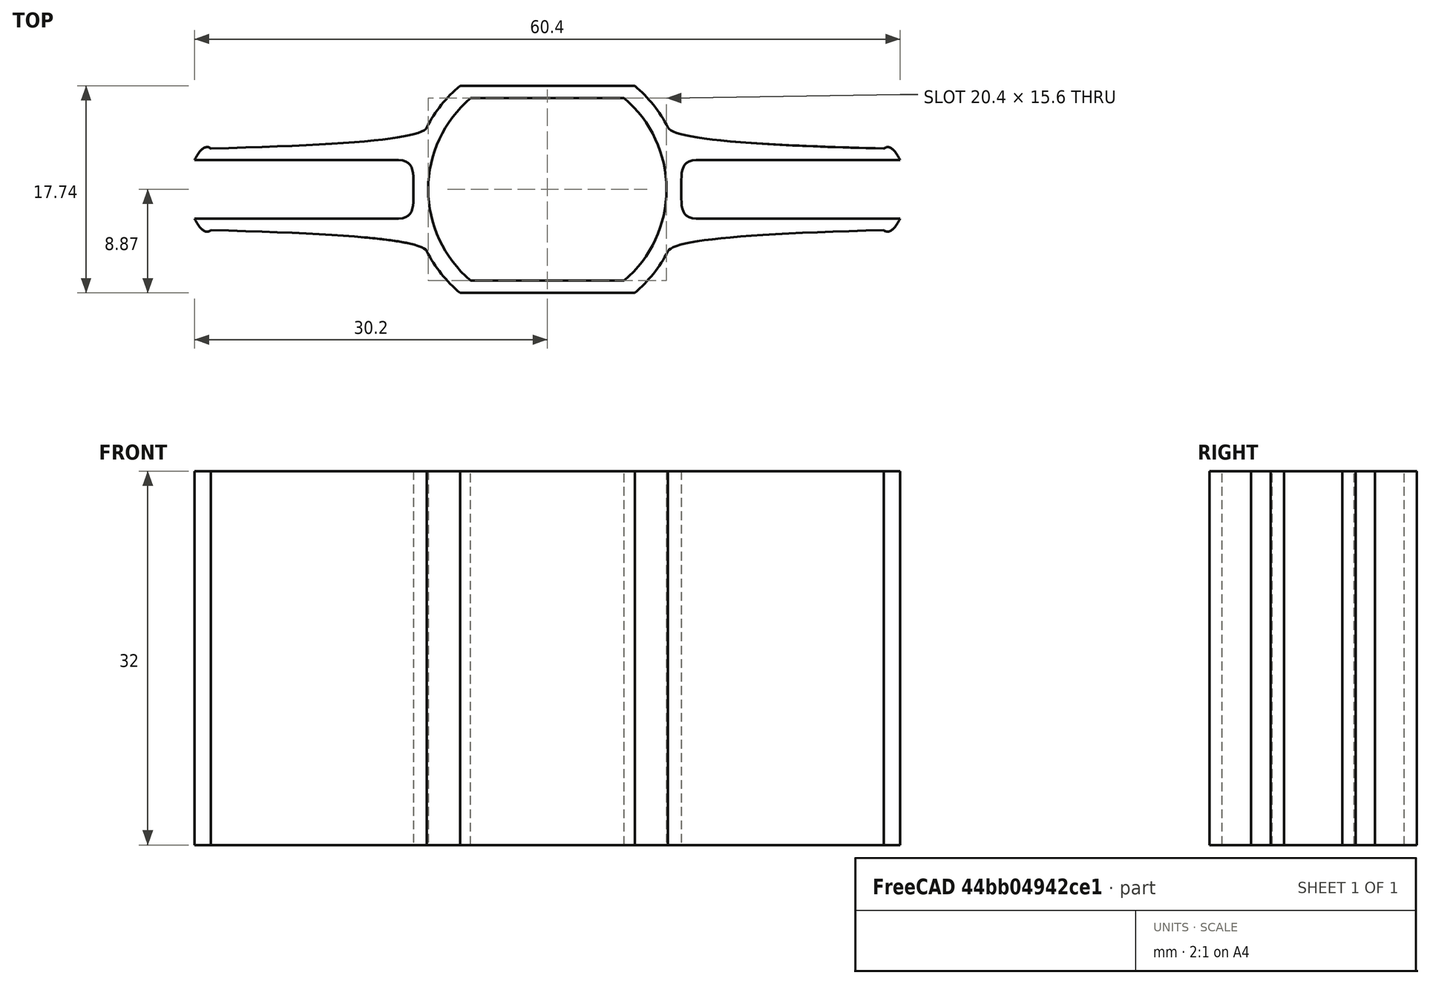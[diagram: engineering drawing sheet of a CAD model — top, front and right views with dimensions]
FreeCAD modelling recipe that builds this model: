
FCSTD DOCUMENT  (FreeCAD 0.19R0.19.2)
Label: 017
License: All rights reserved
LicenseURL: http://en.wikipedia.org/wiki/All_rights_reserved
objects: Sketcher::SketchObject×2, Part::Extrusion×1
note: 3 computed .brp shape members not serialized (recipe doc carries the construction recipe); baked Part::Feature solids carry a one-line shape summary decoded from their .brp

FEATURE [Sketcher::SketchObject] Sketch  label="main001"
  FullyConstrained = true
  sketch-geometry (80):
    g0: ArcOfCircle CenterX=-3.45031e-07 CenterY=0 CenterZ=0 NormalX=0 NormalY=0 NormalZ=1 AngleXU=0 Radius=10.2 StartAngle=5.4126 EndAngle=7.15377
    g1: ArcOfCircle CenterX=-3.45031e-07 CenterY=0 CenterZ=0 NormalX=0 NormalY=0 NormalZ=1 AngleXU=0 Radius=10.2 StartAngle=2.27101 EndAngle=4.01218
    g2: LineSegment StartX=-6.57267 StartY=7.8 StartZ=0 EndX=6.57267 EndY=7.8 EndZ=0
    g3: LineSegment StartX=-6.57267 StartY=-7.8 StartZ=0 EndX=6.57267 EndY=-7.8 EndZ=0
    g4: ArcOfCircle CenterX=-3.45031e-07 CenterY=0 CenterZ=0 NormalX=0 NormalY=0 NormalZ=1 AngleXU=0 Radius=11.6 StartAngle=2.27101 EndAngle=2.66709
    g5: ArcOfCircle CenterX=-3.45031e-07 CenterY=0 CenterZ=0 NormalX=0 NormalY=0 NormalZ=1 AngleXU=0 Radius=11.6 StartAngle=5.4126 EndAngle=5.80868
    g6: LineSegment StartX=-7.4748 StartY=8.87059 StartZ=0 EndX=7.4748 EndY=8.87059 EndZ=0
    g7: LineSegment StartX=-7.4748 StartY=-8.87059 StartZ=0 EndX=7.4748 EndY=-8.87059 EndZ=0
    g8: ArcOfCircle CenterX=-3.45031e-07 CenterY=0 CenterZ=0 NormalX=0 NormalY=0 NormalZ=1 AngleXU=0 Radius=11.6 StartAngle=3.6161 EndAngle=4.01218
    g9: ArcOfCircle CenterX=-3.45031e-07 CenterY=0 CenterZ=0 NormalX=0 NormalY=0 NormalZ=1 AngleXU=0 Radius=11.6 StartAngle=0.474503 EndAngle=0.870585
    g10: Circle CenterX=-28.8 CenterY=3.5 CenterZ=0 NormalX=0 NormalY=0 NormalZ=1 AngleXU=0 Radius=1
    g11: Circle CenterX=-10.9247 CenterY=3.9 CenterZ=0 NormalX=0 NormalY=0 NormalZ=1 AngleXU=0 Radius=1
    g12: Circle CenterX=-10.3184 CenterY=5.3 CenterZ=0 NormalX=0 NormalY=0 NormalZ=1 AngleXU=0 Radius=1
    g13: BSplineCurve PolesCount=3 KnotsCount=2 Degree=2 IsPeriodic=0
    g14: GeomPoint X=-28.8 Y=3.5 Z=0
    g15: GeomPoint X=-10.3184 Y=5.3 Z=0
    g16: Circle CenterX=28.8 CenterY=3.5 CenterZ=0 NormalX=0 NormalY=0 NormalZ=1 AngleXU=0 Radius=1
    g17: Circle CenterX=10.9247 CenterY=3.9 CenterZ=0 NormalX=0 NormalY=0 NormalZ=1 AngleXU=0 Radius=1
    g18: Circle CenterX=10.3184 CenterY=5.3 CenterZ=0 NormalX=0 NormalY=0 NormalZ=1 AngleXU=0 Radius=1
    g19: BSplineCurve PolesCount=3 KnotsCount=2 Degree=2 IsPeriodic=0
    g20: GeomPoint X=28.8 Y=3.5 Z=0
    g21: GeomPoint X=10.3184 Y=5.3 Z=0
    g22: Circle CenterX=-28.8 CenterY=-3.5 CenterZ=0 NormalX=0 NormalY=0 NormalZ=1 AngleXU=0 Radius=1
    g23: Circle CenterX=-10.9247 CenterY=-3.9 CenterZ=0 NormalX=0 NormalY=0 NormalZ=1 AngleXU=0 Radius=1
    g24: Circle CenterX=-10.3184 CenterY=-5.3 CenterZ=0 NormalX=0 NormalY=0 NormalZ=1 AngleXU=0 Radius=1
    g25: BSplineCurve PolesCount=3 KnotsCount=2 Degree=2 IsPeriodic=0
    g26: GeomPoint X=-28.8 Y=-3.5 Z=0
    g27: GeomPoint X=-10.3184 Y=-5.3 Z=0
    g28: Circle CenterX=28.8 CenterY=-3.5 CenterZ=0 NormalX=0 NormalY=0 NormalZ=1 AngleXU=0 Radius=1
    g29: Circle CenterX=10.9247 CenterY=-3.9 CenterZ=0 NormalX=0 NormalY=0 NormalZ=1 AngleXU=0 Radius=1
    g30: Circle CenterX=10.3184 CenterY=-5.3 CenterZ=0 NormalX=0 NormalY=0 NormalZ=1 AngleXU=0 Radius=1
    g31: BSplineCurve PolesCount=3 KnotsCount=2 Degree=2 IsPeriodic=0
    g32: GeomPoint X=28.8 Y=-3.5 Z=0
    g33: GeomPoint X=10.3184 Y=-5.3 Z=0
    g34-g38: Circle x5 (B-spline internal-alignment scaffolding for g39; pole/knot coordinates omitted)
    g39: BSplineCurve PolesCount=5 KnotsCount=3 Degree=3 IsPeriodic=0
    g40: GeomPoint X=12.7274 Y=2.5 Z=0
    g41: GeomPoint X=11.4637 Y=2.49999e-07 Z=0
    g42: GeomPoint X=12.7274 Y=-2.5 Z=0
    g43-g47: Circle x5 (B-spline internal-alignment scaffolding for g48; pole/knot coordinates omitted)
    g48: BSplineCurve PolesCount=5 KnotsCount=3 Degree=3 IsPeriodic=0
    g49: GeomPoint X=-12.7274 Y=2.5 Z=0
    g50: GeomPoint X=-11.4637 Y=2.50004e-07 Z=0
    g51: GeomPoint X=-12.7274 Y=-2.5 Z=0
    g52: LineSegment StartX=-30.2 StartY=-2.5 StartZ=0 EndX=-12.7274 EndY=-2.5 EndZ=0
    g53: LineSegment StartX=-30.2 StartY=2.5 StartZ=0 EndX=-12.7274 EndY=2.5 EndZ=0
    g54: LineSegment StartX=30.2 StartY=2.5 StartZ=0 EndX=12.7274 EndY=2.5 EndZ=0
    g55: LineSegment StartX=30.2 StartY=-2.5 StartZ=0 EndX=12.7274 EndY=-2.5 EndZ=0
    g56: Circle CenterX=-30.2 CenterY=2.5 CenterZ=0 NormalX=0 NormalY=0 NormalZ=1 AngleXU=0 Radius=1
    g57: Circle CenterX=-29.4304 CenterY=3.99253 CenterZ=0 NormalX=0 NormalY=0 NormalZ=1 AngleXU=0 Radius=1
    g58: Circle CenterX=-28.8 CenterY=3.5 CenterZ=0 NormalX=0 NormalY=0 NormalZ=1 AngleXU=0 Radius=1
    g59: BSplineCurve PolesCount=3 KnotsCount=2 Degree=2 IsPeriodic=0
    g60: GeomPoint X=-30.2 Y=2.5 Z=0
    g61: GeomPoint X=-28.8 Y=3.5 Z=0
    g62: Circle CenterX=30.2 CenterY=-2.5 CenterZ=0 NormalX=0 NormalY=0 NormalZ=1 AngleXU=0 Radius=1
    g63: Circle CenterX=29.4304 CenterY=-3.99253 CenterZ=0 NormalX=0 NormalY=0 NormalZ=1 AngleXU=0 Radius=1
    g64: Circle CenterX=28.8 CenterY=-3.5 CenterZ=0 NormalX=0 NormalY=0 NormalZ=1 AngleXU=0 Radius=1
    g65: BSplineCurve PolesCount=3 KnotsCount=2 Degree=2 IsPeriodic=0
    g66: GeomPoint X=30.2 Y=-2.5 Z=0
    g67: GeomPoint X=28.8 Y=-3.5 Z=0
    g68: Circle CenterX=30.2 CenterY=2.5 CenterZ=0 NormalX=0 NormalY=0 NormalZ=1 AngleXU=0 Radius=1
    g69: Circle CenterX=29.4304 CenterY=3.99253 CenterZ=0 NormalX=0 NormalY=0 NormalZ=1 AngleXU=0 Radius=1
    g70: Circle CenterX=28.8 CenterY=3.5 CenterZ=0 NormalX=0 NormalY=0 NormalZ=1 AngleXU=0 Radius=1
    g71: BSplineCurve PolesCount=3 KnotsCount=2 Degree=2 IsPeriodic=0
    g72: GeomPoint X=30.2 Y=2.5 Z=0
    g73: GeomPoint X=28.8 Y=3.5 Z=0
    g74: Circle CenterX=-30.2 CenterY=-2.5 CenterZ=0 NormalX=0 NormalY=0 NormalZ=1 AngleXU=0 Radius=1
    g75: Circle CenterX=-29.4304 CenterY=-3.99253 CenterZ=0 NormalX=0 NormalY=0 NormalZ=1 AngleXU=0 Radius=1
    g76: Circle CenterX=-28.8 CenterY=-3.5 CenterZ=0 NormalX=0 NormalY=0 NormalZ=1 AngleXU=0 Radius=1
    g77: BSplineCurve PolesCount=3 KnotsCount=2 Degree=2 IsPeriodic=0
    g78: GeomPoint X=-30.2 Y=-2.5 Z=0
    g79: GeomPoint X=-28.8 Y=-3.5 Z=0
  constraints (131):
    c: Block(g0)
    c: Equal(g0,g1)
    c: Coincident(g0,g1)
    c: Coincident(g2,g1)
    c: Coincident(g2,g0)
    c: Horizontal(g2)
    c: Coincident(g3,g1)
    c: Coincident(g3,g0)
    c: Horizontal(g3)
    c: Block(g2)
    c: Block(g3)
    c: Coincident(g4,g0)
    c: Coincident(g5,g0)
    c: Block(g5)
    c: Block(g4)
    c: Coincident(g6,g4)
    c: Coincident(g6,g9)
    c: Horizontal(g6)
    c: Coincident(g7,g8)
    c: Coincident(g7,g5)
    c: Horizontal(g7)
    c: Equal(g4,g8)
    c: Coincident(g4,g8)
    c: Equal(g5,g9)
    c: Coincident(g5,g9)
    c: Block(g8)
    c: Block(g9)
    c: Weight(g10) = 1
    c: Equal(g10,g11)
    c: Equal(g10,g12)
    c: Coincident(g13,g4)
    c: InternalAlignment(g10,g13)
    c: InternalAlignment(g11,g13)
    c: InternalAlignment(g12,g13)
    c: InternalAlignment(g14,g13)
    c: InternalAlignment(g15,g13)
    c: Weight(g16) = 1
    c: Equal(g16,g17)
    c: Equal(g16,g18)
    c: Coincident(g19,g9)
    c: InternalAlignment(g16,g19)
    c: InternalAlignment(g17,g19)
    c: InternalAlignment(g18,g19)
    c: InternalAlignment(g20,g19)
    c: InternalAlignment(g21,g19)
    c: Weight(g22) = 1
    c: Equal(g22,g23)
    c: Equal(g22,g24)
    c: Coincident(g25,g8)
    c: InternalAlignment(g22,g25)
    c: InternalAlignment(g23,g25)
    c: InternalAlignment(g24,g25)
    c: InternalAlignment(g26,g25)
    c: InternalAlignment(g27,g25)
    c: Weight(g28) = 1
    c: Equal(g28,g29)
    c: Equal(g28,g30)
    c: Coincident(g31,g5)
    c: InternalAlignment(g28,g31)
    c: InternalAlignment(g29,g31)
    c: InternalAlignment(g30,g31)
    c: InternalAlignment(g32,g31)
    c: InternalAlignment(g33,g31)
    c: Block(g19)
    c: Block(g13)
    c: Block(g31)
    c: Block(g25)
    c: Weight(g34) = 1
    c: Equal(g34, g35-g38) x4
    c: InternalAlignment(g34-g38 -> g39) x5
    c: InternalAlignment(g40,g39)
    c: InternalAlignment(g41,g39)
    c: InternalAlignment(g42,g39)
    c: Weight(g43) = 1
    c: Equal(g43,g44)
    c: Equal(g43,g45)
    c: Equal(g43,g46)
    c: InternalAlignment(g43-g47 -> g48) x5
    c: InternalAlignment(g49,g48)
    c: InternalAlignment(g50,g48)
    c: InternalAlignment(g51,g48)
    c: Block(g48)
    c: Block(g39)
    c: Coincident(g52,g48)
    c: Tangent(g52,g22)
    c: Coincident(g53,g48)
    c: Tangent(g53,g10)
    c: Coincident(g54,g39)
    c: Tangent(g54,g16)
    c: Coincident(g55,g39)
    c: Tangent(g55,g28)
    c: Weight(g56) = 1
    c: Equal(g56,g57)
    c: Equal(g56,g58)
    c: InternalAlignment(g56,g59)
    c: InternalAlignment(g57,g59)
    c: InternalAlignment(g58,g59)
    c: InternalAlignment(g60,g59)
    c: InternalAlignment(g61,g59)
    c: Weight(g62) = 1
    c: Equal(g62,g63)
    c: Equal(g62,g64)
    c: InternalAlignment(g62,g65)
    c: InternalAlignment(g63,g65)
    c: InternalAlignment(g64,g65)
    c: InternalAlignment(g66,g65)
    c: InternalAlignment(g67,g65)
    c: Weight(g68) = 1
    c: Equal(g68,g69)
    c: Equal(g68,g70)
    c: InternalAlignment(g68,g71)
    c: InternalAlignment(g69,g71)
    c: InternalAlignment(g70,g71)
    c: InternalAlignment(g72,g71)
    c: InternalAlignment(g73,g71)
    c: Block(g71)
    c: Block(g54)
    c: Block(g65)
    c: Block(g55)
    c: Weight(g74) = 1
    c: Equal(g74,g75)
    c: Equal(g74,g76)
    c: InternalAlignment(g74,g77)
    c: InternalAlignment(g75,g77)
    c: InternalAlignment(g76,g77)
    c: InternalAlignment(g78,g77)
    c: InternalAlignment(g79,g77)
    c: Block(g77)
    c: Block(g52)
    c: Block(g59)
    c: Block(g53)
FEATURE [Part::Extrusion] Extrude  label="main"
  Base = -> Sketch
  Dir = (0,0,1)
  DirMode = 2
  FaceMakerClass = Part::FaceMakerBullseye
  LengthFwd = 32
  LengthRev = 0
  Solid = true
  Symmetric = false
FEATURE [Sketcher::SketchObject] Sketch001  label="mainCollingAndStructuralHoles"
  FullyConstrained = true
  Placement = pos=(0,0,0) rot=(-1,0,0;4.71239rad)
  sketch-geometry (19):
    g0: Circle CenterX=-5 CenterY=2 CenterZ=0 NormalX=0 NormalY=0 NormalZ=1 AngleXU=0 Radius=1
    g1: Circle CenterX=-5 CenterY=0 CenterZ=0 NormalX=0 NormalY=0 NormalZ=1 AngleXU=0 Radius=1
    g2: Circle CenterX=-3 CenterY=4.6505e-12 CenterZ=0 NormalX=0 NormalY=0 NormalZ=1 AngleXU=0 Radius=1
    g3: BSplineCurve PolesCount=3 KnotsCount=2 Degree=2 IsPeriodic=0
    g4: GeomPoint X=-5 Y=2 Z=0
    g5: GeomPoint X=-3 Y=4.6505e-12 Z=0
    g6: Circle CenterX=5 CenterY=2 CenterZ=0 NormalX=0 NormalY=0 NormalZ=1 AngleXU=0 Radius=1
    g7: Circle CenterX=5 CenterY=4.6505e-12 CenterZ=0 NormalX=0 NormalY=0 NormalZ=1 AngleXU=0 Radius=1
    g8: Circle CenterX=3 CenterY=4.6505e-12 CenterZ=0 NormalX=0 NormalY=0 NormalZ=1 AngleXU=0 Radius=1
    g9: BSplineCurve PolesCount=3 KnotsCount=2 Degree=2 IsPeriodic=0
    g10: GeomPoint X=5 Y=2 Z=0
    g11: GeomPoint X=3 Y=4.6505e-12 Z=0
    g12: LineSegment StartX=5 StartY=2 StartZ=0 EndX=5 EndY=10 EndZ=0
    g13: LineSegment StartX=-5 StartY=2 StartZ=0 EndX=-5 EndY=10 EndZ=0
    g14: LineSegment StartX=-3 StartY=4.6505e-12 StartZ=0 EndX=3 EndY=4.6505e-12 EndZ=0
    g15: LineSegment StartX=-5 StartY=10 StartZ=0 EndX=5 EndY=10 EndZ=0
    g16: LineSegment StartX=-5 StartY=-7 StartZ=0 EndX=5 EndY=-7 EndZ=0
    g17: LineSegment StartX=-5 StartY=-7 StartZ=0 EndX=-5 EndY=-16 EndZ=0
    g18: LineSegment StartX=-5 StartY=-16 StartZ=0 EndX=5 EndY=-16 EndZ=0
  constraints (39):
    c: Weight(g0) = 1
    c: Equal(g0,g1)
    c: Equal(g0,g2)
    c: InternalAlignment(g0,g3)
    c: InternalAlignment(g1,g3)
    c: InternalAlignment(g2,g3)
    c: InternalAlignment(g4,g3)
    c: InternalAlignment(g5,g3)
    c: Weight(g6) = 1
    c: Equal(g6,g7)
    c: Equal(g6,g8)
    c: InternalAlignment(g6,g9)
    c: InternalAlignment(g7,g9)
    c: InternalAlignment(g8,g9)
    c: InternalAlignment(g10,g9)
    c: InternalAlignment(g11,g9)
    c: Block(g3)
    c: Coincident(g13,g3)
    c: Block(g9)
    c: Coincident(g12,g9)
    c: Vertical(g12)
    c: Block(g12)
    c: Block(g13)
    c: Coincident(g14,g3)
    c: Coincident(g14,g9)
    c: Horizontal(g14)
    c: Coincident(g15,g13)
    c: Coincident(g15,g12)
    c: Horizontal(g15)
    c: Distance(g12) = 8
    c: Distance(g15) = 10
    c: Horizontal(g16)
    c: Equal(g15,g16) = 10
    c: Vertical(g17)
    c: Distance(g17) = 9
    c: Horizontal(g18)
    c: Coincident(g18,g17)
    c: Block(g18)
    c: Block(g16)
